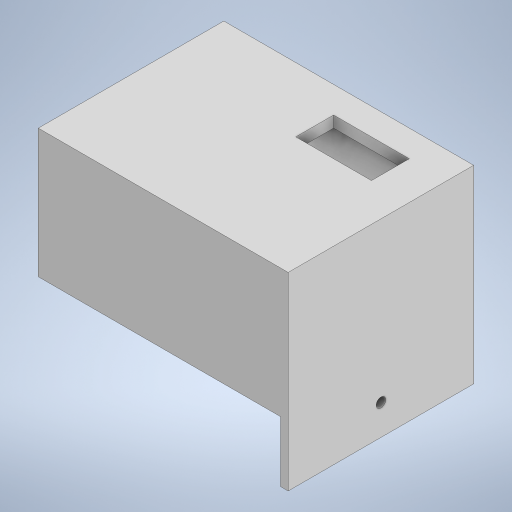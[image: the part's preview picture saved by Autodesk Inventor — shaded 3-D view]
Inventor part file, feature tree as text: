
AUTODESK INVENTOR PART (.ipt)
format: ipt  version: 2024 (Build 280153000, 153)  size: 245,248 bytes
history: native  units: in
note: dims shown in document units (in); Inventor stores cm internally (conversion verified against a paired STEP export)
features: extrude x7, sketch x7
ambient origin geometry x8: Origin, YZ Plane, XZ Plane, XY Plane, X Axis, Y Axis, Z Axis, Center Point
bodies: Body1 (feature_tree)
feature tree (14):
  extrude  "Extrusion51"  Depth=1.9291in
  extrude  "Extrusion52"  Depth=0.1181in
  extrude  "Extrusion53"  Depth=0.1181in
  extrude  "Extrusion54"  Depth=0.315in
  extrude  "Extrusion55"  Depth=0.7874in
  extrude  "Extrusion56"  Depth=1.2205in TaperAngle=0.0deg
  extrude  "Extrusion57"  Depth=1.9291in
  sketch  "Sketch94"  dims[d270=2.5197in d271=1.9291in]
  sketch  "Sketch96"  dims[d272=0.1181in d273=0.0in d274=0.1181in]
  sketch  "Sketch97"  dims[d275=1.2205in d276=0.0in d277=0.1181in]
  sketch  "Sketch98"  dims[d278=1.2205in d279=0.0in d280=0.315in]
  sketch  "Sketch99"  dims[d281=0.2756in d282=0.7874in]
  sketch  "Sketch100"  dims[d283=0.3937in d284=1.2205in d285=0.0in]
  sketch  "Sketch101"  dims[d286=0.0787in d287=1.9291in d288=1.9685in d289=0.0in d290=0.1181in d291=0.5118in d292=0.0in d293=0.9646in d294=0.315in d295=0.0984in d296=0.5118in d297=0.0in d42=0.0197in d43=0.0344in d44=0.0197in d45=0.0344in d46=0.0in d47=0.0in d48=0.0in d49=0.0in d50=0.0in d51=0.0in d52=0.0in d53=0.0in d55=0.0197in d56=0.0344in d57=0.0197in d58=0.0344in d60=0.0197in d61=0.0344in d62=0.0197in d63=0.0344in d72=0.0197in d73=0.0344in d74=0.0197in d75=0.0344in d179=0.0197in d180=0.0344in d181=0.0197in d182=0.0344in d211=0.0197in d212=0.0344in d213=0.0197in d214=0.0344in d235=0.0197in d236=0.0344in d237=0.0197in d238=0.0344in d243=0.0197in d244=0.0344in d245=0.0197in d246=0.0344in]
